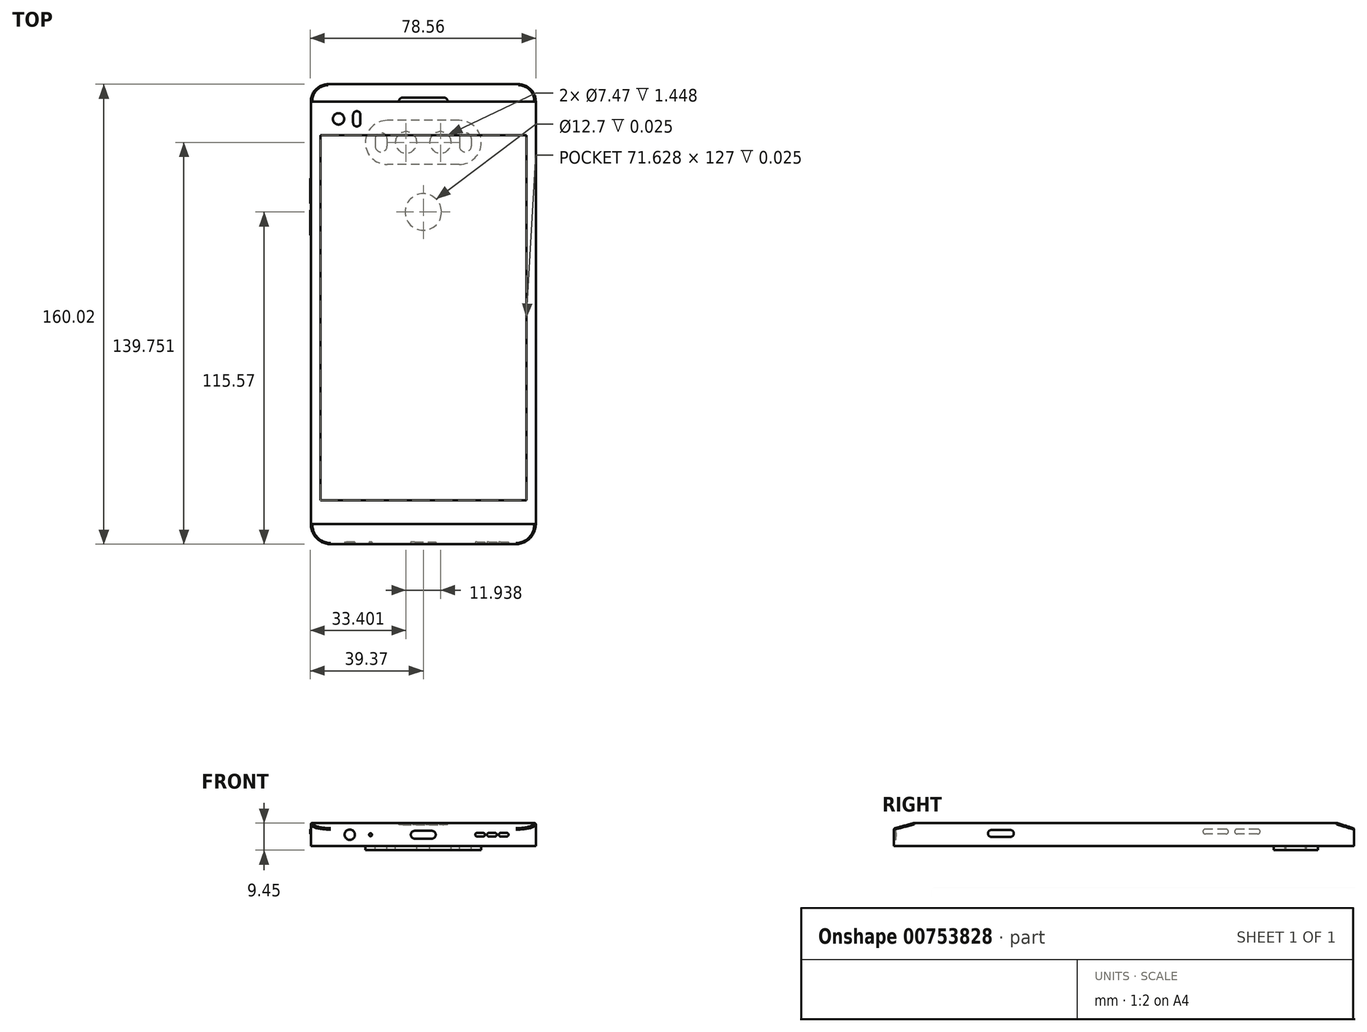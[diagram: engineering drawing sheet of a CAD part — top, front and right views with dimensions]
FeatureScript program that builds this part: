
annotation { "Feature Type Name" : "Feature", "Feature Type Description" : "" }
export const myFeature = defineFeature(function(context is Context, id is Id, definition is map)
    precondition{}
    {
        {
            var Q0;
            Q0=qCreatedBy(makeId("Top.planeOp"),FACE);
            var sketch = newSketch(context, id + "F0", { "sketchPlane" : qUnion([Q0])});
            skLineSegment(sketch, "E0.bottom", {"start": v(-39.12, 73.52) * mm, "end": v(39.12, 73.52) * mm});
            skLineSegment(sketch, "E0.top", {"start": v(-39.12, -73.52) * mm, "end": v(39.12, -73.52) * mm});
            skLineSegment(sketch, "E0.left", {"start": v(-39.12, 73.52) * mm, "end": v(-39.12, -73.52) * mm});
            skLineSegment(sketch, "E0.right", {"start": v(39.12, 73.52) * mm, "end": v(39.12, -73.52) * mm});
            skLineSegment(sketch, "E1", {"start": v(-32.16, -80.48) * mm, "end": v(32.16, -80.48) * mm});
            skLineSegment(sketch, "E2", {"start": v(-33.1, 79.54) * mm, "end": v(33.1, 79.54) * mm});
            skArc(sketch, "E3", {"start": v(-33.1, 79.54) * mm, "mid": v(-37.35, 77.78) * mm, "end": v(-39.12, 73.52) * mm});
            skArc(sketch, "E4", {"start": v(39.12, 73.52) * mm, "mid": v(37.35, 77.78) * mm, "end": v(33.1, 79.54) * mm});
            skArc(sketch, "E5", {"start": v(-39.12, -73.52) * mm, "mid": v(-37.08, -78.44) * mm, "end": v(-32.16, -80.48) * mm});
            skArc(sketch, "E6", {"start": v(32.16, -80.48) * mm, "mid": v(37.08, -78.44) * mm, "end": v(39.12, -73.52) * mm});
            skSolve(sketch);
        }
        {
            var Q0;
            Q0=makeQuery(id+"F0.imprint","IMPRINT",FACE,{"disambiguationData":[TD([[makeQuery(id+"F0.imprint","IMPRINT",EDGE,{"derivedFrom":sQuery(id+"F0.wireOp",EDGE,"E0.bottom")}),-1.0]])]});
            var Q1;
            Q1=makeQuery(id+"F0.imprint","IMPRINT",FACE,{"disambiguationData":[TD([[makeQuery(id+"F0.imprint","IMPRINT",EDGE,{"derivedFrom":sQuery(id+"F0.wireOp",EDGE,"E0.top")}),-1.0]])]});
            var Q2;
            Q2=makeQuery(id+"F0.imprint","IMPRINT",FACE,{"disambiguationData":[TD([[makeQuery(id+"F0.imprint","IMPRINT",EDGE,{"derivedFrom":sQuery(id+"F0.wireOp",EDGE,"E0.bottom")}),1.0]])]});
            extrude(context, id + "F1", {"entities" : qUnion([Q0, Q1, Q2]), "oppositeDirection" : true, "depth" : 8 * mm, "offsetDistance" : 25.4 * mm});
        }
        {
            var Q0;
            Q0=makeQuery(id+"F1.opExtrude","CAP_FACE",FACE,{"disambiguationData":[OSD([sQuery(id+"F0.wireOp",EDGE,"E0.left"),sQuery(id+"F0.wireOp",EDGE,"E0.right"),sQuery(id+"F0.wireOp",EDGE,"E1"),sQuery(id+"F0.wireOp",EDGE,"E2"),sQuery(id+"F0.wireOp",EDGE,"E3"),sQuery(id+"F0.wireOp",EDGE,"E4"),sQuery(id+"F0.wireOp",EDGE,"E5"),sQuery(id+"F0.wireOp",EDGE,"E6")])],"isStart":true});
            var sketch = newSketch(context, id + "F2", { "sketchPlane" : qUnion([Q0])});
            skLineSegment(sketch, "E7.bottom", {"start": v(-35.81, 61.76) * mm, "end": v(35.81, 61.76) * mm});
            skLineSegment(sketch, "E7.top", {"start": v(-35.81, -65.24) * mm, "end": v(35.81, -65.24) * mm});
            skLineSegment(sketch, "E7.left", {"start": v(-35.81, 61.76) * mm, "end": v(-35.81, -65.24) * mm});
            skLineSegment(sketch, "E7.right", {"start": v(35.81, 61.76) * mm, "end": v(35.81, -65.24) * mm});
            skLineSegment(sketch, "E8", {"start": v(-35.81, -65.24) * mm, "end": v(35.81, 61.76) * mm, "construction": true});
            skSolve(sketch);
        }
        {
            var Q0;
            Q0=makeQuery(id+"F1.opExtrude","CAP_FACE",FACE,{"disambiguationData":[OSD([sQuery(id+"F0.wireOp",EDGE,"E0.left"),sQuery(id+"F0.wireOp",EDGE,"E0.right"),sQuery(id+"F0.wireOp",EDGE,"E1"),sQuery(id+"F0.wireOp",EDGE,"E2"),sQuery(id+"F0.wireOp",EDGE,"E3"),sQuery(id+"F0.wireOp",EDGE,"E4"),sQuery(id+"F0.wireOp",EDGE,"E5"),sQuery(id+"F0.wireOp",EDGE,"E6")])],"isStart":false});
            var sketch = newSketch(context, id + "F3", { "sketchPlane" : qUnion([Q0])});
            skLineSegment(sketch, "E9", {"start": v(-39.12, 73.52) * mm, "end": v(39.12, 73.52) * mm});
            skLineSegment(sketch, "E10", {"start": v(-39.12, -73.52) * mm, "end": v(39.12, -73.52) * mm});
            skSolve(sketch);
        }
        {
            var Q0;
            Q0=qCreatedBy(makeId("Right.planeOp"),FACE);
            var sketch = newSketch(context, id + "F4", { "sketchPlane" : qUnion([Q0])});
            skLineSegment(sketch, "E11", {"start": v(-73.52, 0) * mm, "end": v(-66.56, 1.9) * mm});
            skLineSegment(sketch, "E12", {"start": v(-73.52, 0) * mm, "end": v(-80.48, -1.9) * mm});
            skLineSegment(sketch, "E13", {"start": v(-80.48, -1.9) * mm, "end": v(-82.16, 4.22) * mm});
            skLineSegment(sketch, "E14", {"start": v(-82.16, 4.22) * mm, "end": v(-68.24, 8.03) * mm});
            skLineSegment(sketch, "E15", {"start": v(-68.24, 8.03) * mm, "end": v(-66.56, 1.9) * mm});
            skLineSegment(sketch, "E16", {"start": v(67.5, 1.9) * mm, "end": v(73.52, 0) * mm});
            skLineSegment(sketch, "E17", {"start": v(73.52, 0) * mm, "end": v(79.54, -1.9) * mm});
            skLineSegment(sketch, "E18", {"start": v(79.54, -1.9) * mm, "end": v(81.46, 4.15) * mm});
            skLineSegment(sketch, "E19", {"start": v(81.46, 4.15) * mm, "end": v(69.42, 7.96) * mm});
            skLineSegment(sketch, "E20", {"start": v(69.42, 7.96) * mm, "end": v(67.5, 1.9) * mm});
            skLineSegment(sketch, "E21", {"start": v(-81.32, -6.63) * mm, "end": v(-73.52, -8) * mm});
            skLineSegment(sketch, "E22", {"start": v(-73.52, -8) * mm, "end": v(-65.73, -9.38) * mm});
            skLineSegment(sketch, "E23", {"start": v(-65.73, -9.38) * mm, "end": v(-66.83, -15.63) * mm});
            skLineSegment(sketch, "E24", {"start": v(-66.83, -15.63) * mm, "end": v(-82.42, -12.88) * mm});
            skLineSegment(sketch, "E25", {"start": v(-82.42, -12.88) * mm, "end": v(-81.32, -6.63) * mm});
            skLineSegment(sketch, "E26", {"start": v(65.73, -9.38) * mm, "end": v(73.52, -8) * mm});
            skLineSegment(sketch, "E27", {"start": v(73.52, -8) * mm, "end": v(81.32, -6.63) * mm});
            skLineSegment(sketch, "E28", {"start": v(81.32, -6.63) * mm, "end": v(82.42, -12.88) * mm});
            skLineSegment(sketch, "E29", {"start": v(82.42, -12.88) * mm, "end": v(66.83, -15.63) * mm});
            skLineSegment(sketch, "E30", {"start": v(66.83, -15.63) * mm, "end": v(65.73, -9.38) * mm});
            skSolve(sketch);
        }
        {
            var Q0;
            Q0=makeQuery(id+"F4.imprint","IMPRINT",FACE,{"disambiguationData":[TD([[makeQuery(id+"F4.imprint","IMPRINT",EDGE,{"derivedFrom":sQuery(id+"F4.wireOp",EDGE,"E11")}),1.0]])]});
            var Q1;
            Q1=makeQuery(id+"F4.imprint","IMPRINT",FACE,{"disambiguationData":[TD([[makeQuery(id+"F4.imprint","IMPRINT",EDGE,{"derivedFrom":sQuery(id+"F4.wireOp",EDGE,"E16")}),1.0]])]});
            extrude(context, id + "F5", {"entities" : qUnion([Q0, Q1]), "operationType" : NewBodyOperationType.REMOVE, "endBound" : BoundingType.SYMMETRIC, "depth" : 101.6 * mm, "offsetDistance" : 25.4 * mm});
        }
        {
            var Q0;
            Q0=makeQuery(id+"F1.opExtrude","CAP_FACE",FACE,{"disambiguationData":[OSD([sQuery(id+"F0.wireOp",EDGE,"E0.left"),sQuery(id+"F0.wireOp",EDGE,"E0.right"),sQuery(id+"F0.wireOp",EDGE,"E1"),sQuery(id+"F0.wireOp",EDGE,"E2"),sQuery(id+"F0.wireOp",EDGE,"E3"),sQuery(id+"F0.wireOp",EDGE,"E4"),sQuery(id+"F0.wireOp",EDGE,"E5"),sQuery(id+"F0.wireOp",EDGE,"E6")])],"isStart":false});
            var sketch = newSketch(context, id + "F6", { "sketchPlane" : qUnion([Q0])});
            skLineSegment(sketch, "E31.bottom", {"start": v(12.48, -66.94) * mm, "end": v(-12.48, -66.94) * mm});
            skLineSegment(sketch, "E31.top", {"start": v(12.48, -51.6) * mm, "end": v(-12.48, -51.6) * mm});
            skLineSegment(sketch, "E31.left", {"start": v(12.48, -66.94) * mm, "end": v(12.48, -51.6) * mm, "construction": true});
            skLineSegment(sketch, "E31.right", {"start": v(-12.48, -66.94) * mm, "end": v(-12.48, -51.6) * mm, "construction": true});
            skArc(sketch, "E32", {"start": v(12.48, -66.94) * mm, "mid": v(20.15, -59.27) * mm, "end": v(12.48, -51.6) * mm});
            skArc(sketch, "E33", {"start": v(-12.48, -51.6) * mm, "mid": v(-20.15, -59.27) * mm, "end": v(-12.48, -66.94) * mm});
            skLineSegment(sketch, "E34", {"start": v(5.97, -59.27) * mm, "end": v(-5.97, -59.27) * mm, "construction": true});
            skCircle(sketch, "E35", {"center": v(5.97, -59.27) * mm, "radius": 3.73 * mm});
            skCircle(sketch, "E36", {"center": v(-5.97, -59.27) * mm, "radius": 3.73 * mm});
            skLineSegment(sketch, "E37.bottom", {"start": v(16.69, -60.58) * mm, "end": v(12.6, -60.58) * mm, "construction": true});
            skLineSegment(sketch, "E37.top", {"start": v(16.69, -57.96) * mm, "end": v(12.6, -57.96) * mm, "construction": true});
            skLineSegment(sketch, "E37.left", {"start": v(16.69, -60.58) * mm, "end": v(16.69, -57.96) * mm});
            skLineSegment(sketch, "E37.right", {"start": v(12.6, -60.58) * mm, "end": v(12.6, -57.96) * mm});
            skLineSegment(sketch, "E38.bottom", {"start": v(-12.6, -60.58) * mm, "end": v(-16.69, -60.58) * mm, "construction": true});
            skLineSegment(sketch, "E38.top", {"start": v(-12.6, -57.96) * mm, "end": v(-16.69, -57.96) * mm, "construction": true});
            skLineSegment(sketch, "E38.left", {"start": v(-12.6, -60.58) * mm, "end": v(-12.6, -57.96) * mm});
            skLineSegment(sketch, "E38.right", {"start": v(-16.69, -60.58) * mm, "end": v(-16.69, -57.96) * mm});
            skArc(sketch, "E39", {"start": v(12.6, -60.58) * mm, "mid": v(14.64, -62.62) * mm, "end": v(16.69, -60.58) * mm});
            skArc(sketch, "E40", {"start": v(16.69, -57.96) * mm, "mid": v(14.64, -55.92) * mm, "end": v(12.6, -57.96) * mm});
            skArc(sketch, "E41", {"start": v(-16.69, -60.58) * mm, "mid": v(-14.64, -62.62) * mm, "end": v(-12.6, -60.58) * mm});
            skArc(sketch, "E42", {"start": v(-12.6, -57.96) * mm, "mid": v(-14.64, -55.92) * mm, "end": v(-16.69, -57.96) * mm});
            skSolve(sketch);
        }
        {
            var Q0;
            Q0=makeQuery(id+"F6.imprint","IMPRINT",FACE,{"disambiguationData":[TD([[makeQuery(id+"F6.imprint","IMPRINT",EDGE,{"derivedFrom":sQuery(id+"F6.wireOp",EDGE,"E31.bottom")}),-1.0]])]});
            extrude(context, id + "F7", {"entities" : qUnion([Q0]), "operationType" : NewBodyOperationType.ADD, "depth" : 1.45 * mm, "offsetDistance" : 25.4 * mm});
        }
        {
            var Q0;
            Q0=makeQuery(id+"F1.opExtrude","SWEPT_FACE",FACE,{"disambiguationData":[OSD([sQuery(id+"F0.wireOp",EDGE,"E1")])]});
            var sketch = newSketch(context, id + "F8", { "sketchPlane" : qUnion([Q0])});
            skCircle(sketch, "E43", {"center": v(-25.57, -4.08) * mm, "radius": 1.8 * mm});
            skLineSegment(sketch, "E44.bottom", {"start": v(-2.97, -2.72) * mm, "end": v(2.97, -2.72) * mm});
            skLineSegment(sketch, "E44.top", {"start": v(-2.97, -5.44) * mm, "end": v(2.97, -5.44) * mm});
            skLineSegment(sketch, "E44.left", {"start": v(-2.97, -2.72) * mm, "end": v(-2.97, -5.44) * mm, "construction": true});
            skLineSegment(sketch, "E44.right", {"start": v(2.97, -2.72) * mm, "end": v(2.97, -5.44) * mm, "construction": true});
            skArc(sketch, "E45", {"start": v(2.97, -5.44) * mm, "mid": v(4.33, -4.08) * mm, "end": v(2.97, -2.72) * mm});
            skArc(sketch, "E46", {"start": v(-2.97, -2.72) * mm, "mid": v(-4.33, -4.08) * mm, "end": v(-2.97, -5.44) * mm});
            skLineSegment(sketch, "E47.bottom", {"start": v(18.7, -3.43) * mm, "end": v(20.82, -3.43) * mm});
            skLineSegment(sketch, "E47.top", {"start": v(18.7, -4.7) * mm, "end": v(20.82, -4.7) * mm});
            skLineSegment(sketch, "E47.left", {"start": v(18.7, -3.43) * mm, "end": v(18.7, -4.7) * mm, "construction": true});
            skLineSegment(sketch, "E47.right", {"start": v(20.82, -3.43) * mm, "end": v(20.82, -4.7) * mm, "construction": true});
            skLineSegment(sketch, "E48.bottom", {"start": v(22.8, -3.43) * mm, "end": v(24.92, -3.43) * mm});
            skLineSegment(sketch, "E48.top", {"start": v(22.8, -4.7) * mm, "end": v(24.92, -4.7) * mm});
            skLineSegment(sketch, "E48.left", {"start": v(22.8, -3.43) * mm, "end": v(22.8, -4.7) * mm, "construction": true});
            skLineSegment(sketch, "E48.right", {"start": v(24.92, -3.43) * mm, "end": v(24.92, -4.7) * mm, "construction": true});
            skLineSegment(sketch, "E49.bottom", {"start": v(26.91, -3.43) * mm, "end": v(29.02, -3.43) * mm});
            skLineSegment(sketch, "E49.top", {"start": v(26.91, -4.7) * mm, "end": v(29.02, -4.7) * mm});
            skLineSegment(sketch, "E49.left", {"start": v(26.91, -3.43) * mm, "end": v(26.91, -4.7) * mm, "construction": true});
            skLineSegment(sketch, "E49.right", {"start": v(29.02, -3.43) * mm, "end": v(29.02, -4.7) * mm, "construction": true});
            skArc(sketch, "E50", {"start": v(20.82, -4.7) * mm, "mid": v(21.45, -4.06) * mm, "end": v(20.82, -3.43) * mm});
            skArc(sketch, "E51", {"start": v(22.8, -3.43) * mm, "mid": v(22.17, -4.06) * mm, "end": v(22.8, -4.7) * mm});
            skArc(sketch, "E52", {"start": v(24.92, -4.7) * mm, "mid": v(25.55, -4.06) * mm, "end": v(24.92, -3.43) * mm});
            skArc(sketch, "E53", {"start": v(26.91, -3.43) * mm, "mid": v(26.28, -4.06) * mm, "end": v(26.91, -4.7) * mm});
            skArc(sketch, "E54", {"start": v(29.02, -4.7) * mm, "mid": v(29.65, -4.06) * mm, "end": v(29.02, -3.43) * mm});
            skArc(sketch, "E55", {"start": v(18.7, -3.43) * mm, "mid": v(18.07, -4.06) * mm, "end": v(18.7, -4.7) * mm});
            skLineSegment(sketch, "E56", {"start": v(20.82, -4.06) * mm, "end": v(22.8, -4.06) * mm, "construction": true});
            skLineSegment(sketch, "E57", {"start": v(24.92, -4.06) * mm, "end": v(26.91, -4.06) * mm, "construction": true});
            skLineSegment(sketch, "E58", {"start": v(-2.97, -4.08) * mm, "end": v(-25.57, -4.08) * mm, "construction": true});
            skCircle(sketch, "E59", {"center": v(-18.33, -4.08) * mm, "radius": 0.5 * mm});
            skSolve(sketch);
        }
        {
            var Q0;
            Q0=makeQuery(id+"F8.imprint","IMPRINT",FACE,{"disambiguationData":[TD([[makeQuery(id+"F8.imprint","IMPRINT",EDGE,{"derivedFrom":sQuery(id+"F8.wireOp",EDGE,"E43")}),1.0]])]});
            var Q1;
            Q1=makeQuery(id+"F8.imprint","IMPRINT",FACE,{"disambiguationData":[TD([[makeQuery(id+"F8.imprint","IMPRINT",EDGE,{"derivedFrom":sQuery(id+"F8.wireOp",EDGE,"E44.bottom")}),-1.0]])]});
            var Q2;
            Q2=makeQuery(id+"F8.imprint","IMPRINT",FACE,{"disambiguationData":[TD([[makeQuery(id+"F8.imprint","IMPRINT",EDGE,{"derivedFrom":sQuery(id+"F8.wireOp",EDGE,"E47.bottom")}),-1.0]])]});
            var Q3;
            Q3=makeQuery(id+"F8.imprint","IMPRINT",FACE,{"disambiguationData":[TD([[makeQuery(id+"F8.imprint","IMPRINT",EDGE,{"derivedFrom":sQuery(id+"F8.wireOp",EDGE,"E48.bottom")}),-1.0]])]});
            var Q4;
            Q4=makeQuery(id+"F8.imprint","IMPRINT",FACE,{"disambiguationData":[TD([[makeQuery(id+"F8.imprint","IMPRINT",EDGE,{"derivedFrom":sQuery(id+"F8.wireOp",EDGE,"E49.bottom")}),-1.0]])]});
            var Q5;
            Q5=makeQuery(id+"F8.imprint","IMPRINT",FACE,{"disambiguationData":[TD([[makeQuery(id+"F8.imprint","IMPRINT",EDGE,{"derivedFrom":sQuery(id+"F8.wireOp",EDGE,"E59")}),1.0]])]});
            extrude(context, id + "F9", {"entities" : qUnion([Q0, Q1, Q2, Q3, Q4, Q5]), "operationType" : NewBodyOperationType.REMOVE, "oppositeDirection" : true, "depth" : 0.76 * mm, "offsetDistance" : 25.4 * mm});
        }
        {
            var Q0;
            Q0=makeQuery(id+"F2.imprint","IMPRINT",FACE,{"disambiguationData":[TD([[makeQuery(id+"F2.imprint","IMPRINT",EDGE,{"derivedFrom":sQuery(id+"F2.wireOp",EDGE,"E7.bottom")}),-1.0]])]});
            extrude(context, id + "F10", {"entities" : qUnion([Q0]), "operationType" : NewBodyOperationType.REMOVE, "oppositeDirection" : true, "depth" : 0.03 * mm, "offsetDistance" : 25.4 * mm});
        }
        {
            var Q0;
            Q0=makeQuery(id+"F1.opExtrude","SWEPT_FACE",FACE,{"disambiguationData":[OSD([sQuery(id+"F0.wireOp",EDGE,"E0.left")])]});
            var sketch = newSketch(context, id + "F11", { "sketchPlane" : qUnion([Q0])});
            skLineSegment(sketch, "E60.bottom", {"start": v(-45.99, -2.13) * mm, "end": v(-38.82, -2.13) * mm});
            skLineSegment(sketch, "E60.top", {"start": v(-45.99, -3.8) * mm, "end": v(-38.82, -3.8) * mm});
            skLineSegment(sketch, "E60.left", {"start": v(-45.99, -2.13) * mm, "end": v(-45.99, -3.8) * mm, "construction": true});
            skLineSegment(sketch, "E60.right", {"start": v(-38.82, -2.13) * mm, "end": v(-38.82, -3.8) * mm, "construction": true});
            skLineSegment(sketch, "E61.bottom", {"start": v(-34.96, -2.13) * mm, "end": v(-27.8, -2.13) * mm});
            skLineSegment(sketch, "E61.top", {"start": v(-34.96, -3.8) * mm, "end": v(-27.8, -3.8) * mm});
            skLineSegment(sketch, "E61.left", {"start": v(-34.96, -2.13) * mm, "end": v(-34.96, -3.8) * mm, "construction": true});
            skLineSegment(sketch, "E61.right", {"start": v(-27.8, -2.13) * mm, "end": v(-27.8, -3.8) * mm, "construction": true});
            skArc(sketch, "E62", {"start": v(-45.99, -2.13) * mm, "mid": v(-46.82, -2.97) * mm, "end": v(-45.99, -3.8) * mm});
            skArc(sketch, "E63", {"start": v(-38.82, -3.8) * mm, "mid": v(-37.99, -2.97) * mm, "end": v(-38.82, -2.13) * mm});
            skArc(sketch, "E64", {"start": v(-34.96, -2.13) * mm, "mid": v(-35.8, -2.97) * mm, "end": v(-34.96, -3.8) * mm});
            skArc(sketch, "E65", {"start": v(-27.8, -3.8) * mm, "mid": v(-26.96, -2.97) * mm, "end": v(-27.8, -2.13) * mm});
            skLineSegment(sketch, "E66", {"start": v(-38.82, -2.97) * mm, "end": v(-34.96, -2.97) * mm, "construction": true});
            skSolve(sketch);
        }
        {
            var Q0;
            Q0=makeQuery(id+"F11.imprint","IMPRINT",FACE,{"disambiguationData":[TD([[makeQuery(id+"F11.imprint","IMPRINT",EDGE,{"derivedFrom":sQuery(id+"F11.wireOp",EDGE,"E60.bottom")}),-1.0]])]});
            var Q1;
            Q1=makeQuery(id+"F11.imprint","IMPRINT",FACE,{"disambiguationData":[TD([[makeQuery(id+"F11.imprint","IMPRINT",EDGE,{"derivedFrom":sQuery(id+"F11.wireOp",EDGE,"E61.bottom")}),-1.0]])]});
            extrude(context, id + "F12", {"entities" : qUnion([Q0, Q1]), "operationType" : NewBodyOperationType.ADD, "depth" : 0.25 * mm, "offsetDistance" : 25.4 * mm});
        }
        {
            var Q0;
            Q0=makeQuery(id+"F1.opExtrude","CAP_FACE",FACE,{"disambiguationData":[OSD([sQuery(id+"F0.wireOp",EDGE,"E0.left"),sQuery(id+"F0.wireOp",EDGE,"E0.right"),sQuery(id+"F0.wireOp",EDGE,"E1"),sQuery(id+"F0.wireOp",EDGE,"E2"),sQuery(id+"F0.wireOp",EDGE,"E3"),sQuery(id+"F0.wireOp",EDGE,"E4"),sQuery(id+"F0.wireOp",EDGE,"E5"),sQuery(id+"F0.wireOp",EDGE,"E6")])],"isStart":true});
            var sketch = newSketch(context, id + "F13", { "sketchPlane" : qUnion([Q0])});
            skCircle(sketch, "E67", {"center": v(-29.46, 67.48) * mm, "radius": 1.98 * mm});
            skLineSegment(sketch, "E68.bottom", {"start": v(-24.38, 68.87) * mm, "end": v(-21.84, 68.87) * mm, "construction": true});
            skLineSegment(sketch, "E68.top", {"start": v(-24.38, 66.08) * mm, "end": v(-21.84, 66.08) * mm, "construction": true});
            skLineSegment(sketch, "E68.left", {"start": v(-24.38, 68.87) * mm, "end": v(-24.38, 66.08) * mm});
            skLineSegment(sketch, "E68.right", {"start": v(-21.84, 68.87) * mm, "end": v(-21.84, 66.08) * mm});
            skArc(sketch, "E69", {"start": v(-21.84, 68.87) * mm, "mid": v(-23.11, 70.14) * mm, "end": v(-24.38, 68.87) * mm});
            skArc(sketch, "E70", {"start": v(-24.38, 66.08) * mm, "mid": v(-23.11, 64.8) * mm, "end": v(-21.84, 66.08) * mm});
            skLineSegment(sketch, "E71", {"start": v(-29.46, 67.48) * mm, "end": v(-24.38, 67.48) * mm, "construction": true});
            skLineSegment(sketch, "E72", {"start": v(-8.47, 73.52) * mm, "end": v(8.47, 73.52) * mm});
            skLineSegment(sketch, "E73", {"start": v(-7.07, 74.92) * mm, "end": v(7.07, 74.92) * mm});
            skLineSegment(sketch, "E74", {"start": v(0, 74.92) * mm, "end": v(0, 73.52) * mm, "construction": true});
            skArc(sketch, "E75", {"start": v(-7.07, 74.92) * mm, "mid": v(-8.06, 74.5) * mm, "end": v(-8.47, 73.52) * mm});
            skArc(sketch, "E76", {"start": v(8.47, 73.52) * mm, "mid": v(8.06, 74.5) * mm, "end": v(7.07, 74.92) * mm});
            skSolve(sketch);
        }
        {
            var Q0;
            Q0=makeQuery(id+"F13.imprint","IMPRINT",FACE,{"disambiguationData":[TD([[makeQuery(id+"F13.imprint","IMPRINT",EDGE,{"derivedFrom":sQuery(id+"F13.wireOp",EDGE,"E67")}),1.0]])]});
            var Q1;
            Q1=makeQuery(id+"F13.imprint","IMPRINT",FACE,{"disambiguationData":[TD([[makeQuery(id+"F13.imprint","IMPRINT",EDGE,{"derivedFrom":sQuery(id+"F13.wireOp",EDGE,"E68.left")}),1.0]])]});
            extrude(context, id + "F14", {"entities" : qUnion([Q0, Q1]), "operationType" : NewBodyOperationType.REMOVE, "oppositeDirection" : true, "depth" : 0.03 * mm, "offsetDistance" : 25.4 * mm});
        }
        {
            var Q0;
            Q0=makeQuery(id+"F13.imprint","IMPRINT",FACE,{"disambiguationData":[TD([[makeQuery(id+"F13.imprint","IMPRINT",EDGE,{"derivedFrom":sQuery(id+"F13.wireOp",EDGE,"E72")}),-1.0]])]});
            extrude(context, id + "F15", {"entities" : qUnion([Q0]), "operationType" : NewBodyOperationType.REMOVE, "oppositeDirection" : true, "depth" : 0.64 * mm, "offsetDistance" : 25.4 * mm});
        }
        {
            var Q0;
            Q0=makeQuery(id+"F1.opExtrude","SWEPT_FACE",FACE,{"disambiguationData":[OSD([sQuery(id+"F0.wireOp",EDGE,"E0.right")])]});
            var sketch = newSketch(context, id + "F16", { "sketchPlane" : qUnion([Q0])});
            skLineSegment(sketch, "E77.bottom", {"start": v(-46.6, -2.44) * mm, "end": v(-40.02, -2.44) * mm});
            skLineSegment(sketch, "E77.top", {"start": v(-46.6, -4.83) * mm, "end": v(-40.02, -4.83) * mm});
            skLineSegment(sketch, "E77.left", {"start": v(-46.6, -2.44) * mm, "end": v(-46.6, -4.83) * mm, "construction": true});
            skLineSegment(sketch, "E77.right", {"start": v(-40.02, -2.44) * mm, "end": v(-40.02, -4.83) * mm, "construction": true});
            skArc(sketch, "E78", {"start": v(-40.02, -4.83) * mm, "mid": v(-38.82, -3.63) * mm, "end": v(-40.02, -2.44) * mm});
            skArc(sketch, "E79", {"start": v(-46.6, -2.44) * mm, "mid": v(-47.8, -3.63) * mm, "end": v(-46.6, -4.83) * mm});
            skSolve(sketch);
        }
        {
            var Q0;
            Q0=makeQuery(id+"F16.imprint","IMPRINT",FACE,{"disambiguationData":[TD([[makeQuery(id+"F16.imprint","IMPRINT",EDGE,{"derivedFrom":sQuery(id+"F16.wireOp",EDGE,"E77.bottom")}),-1.0]])]});
            extrude(context, id + "F17", {"entities" : qUnion([Q0]), "operationType" : NewBodyOperationType.ADD, "depth" : 0.08 * mm, "offsetDistance" : 25.4 * mm});
        }
        {
            var Q0;
            {var subQ0=sQuery(id+"F0.wireOp",EDGE,"E0.left");var subQ1=sQuery(id+"F0.wireOp",EDGE,"E6");var subQ2=sQuery(id+"F0.wireOp",EDGE,"E5");var subQ3=sQuery(id+"F0.wireOp",EDGE,"E0.right");var subQ4=sQuery(id+"F0.wireOp",EDGE,"E3");var subQ5=sQuery(id+"F0.wireOp",EDGE,"E4");Q0=makeQuery(id+"F7.boolean.opBoolean","SPLIT",FACE,{"disambiguationData":[TD([makeQuery(id+"F1.opExtrude","SWEPT_FACE",FACE,{"disambiguationData":[OSD([subQ0])]})])],"derivedFrom":makeQuery(id+"F1.opExtrude","CAP_FACE",FACE,{"disambiguationData":[OSD([subQ0,subQ3,sQuery(id+"F0.wireOp",EDGE,"E1"),sQuery(id+"F0.wireOp",EDGE,"E2"),subQ4,subQ5,subQ2,subQ1])],"isStart":false})});}
            var sketch = newSketch(context, id + "F18", { "sketchPlane" : qUnion([Q0])});
            skCircle(sketch, "E80", {"center": v(0, -35.1) * mm, "radius": 6.35 * mm});
            skSolve(sketch);
        }
        {
            var Q0;
            Q0=makeQuery(id+"F18.imprint","IMPRINT",FACE,{"disambiguationData":[TD([[makeQuery(id+"F18.imprint","IMPRINT",EDGE,{"derivedFrom":sQuery(id+"F18.wireOp",EDGE,"E80")}),1.0]])]});
            extrude(context, id + "F19", {"entities" : qUnion([Q0]), "operationType" : NewBodyOperationType.REMOVE, "oppositeDirection" : true, "depth" : 0.03 * mm, "offsetDistance" : 25.4 * mm});
        }
        {
            var Q0;
            Q0=makeQuery(id+"F5.boolean.opBoolean","INTERSECT",EDGE,{"derivedFrom":[makeQuery(id+"F1.opExtrude","SWEPT_FACE",FACE,{"disambiguationData":[OSD([sQuery(id+"F0.wireOp",EDGE,"E6")])]}),makeQuery(id+"F5.opExtrude","SWEPT_FACE",FACE,{"disambiguationData":[OSD([sQuery(id+"F4.wireOp",EDGE,"E11"),sQuery(id+"F4.wireOp",EDGE,"E12")])]})]});
            var Q1;
            Q1=makeQuery(id+"F1.opExtrude","CAP_EDGE",EDGE,{"disambiguationData":[OSD([sQuery(id+"F0.wireOp",EDGE,"E0.right")])],"isStart":true});
            var Q2;
            Q2=makeQuery(id+"F1.opExtrude","CAP_EDGE",EDGE,{"disambiguationData":[OSD([sQuery(id+"F0.wireOp",EDGE,"E0.left")])],"isStart":true});
            var Q3;
            Q3=makeQuery(id+"F5.boolean.opBoolean","INTERSECT",EDGE,{"derivedFrom":[makeQuery(id+"F1.opExtrude","SWEPT_FACE",FACE,{"disambiguationData":[OSD([sQuery(id+"F0.wireOp",EDGE,"E4")])]}),makeQuery(id+"F5.opExtrude","SWEPT_FACE",FACE,{"disambiguationData":[OSD([sQuery(id+"F4.wireOp",EDGE,"E16"),sQuery(id+"F4.wireOp",EDGE,"E17")])]})]});
            fillet(context, id + "F20", {"entities" : qUnion([Q0, Q1, Q2, Q3]), "radius" : 0.5 * mm, "tangentPropagation" : true, "allowEdgeOverflow" : false});
        }
    });
